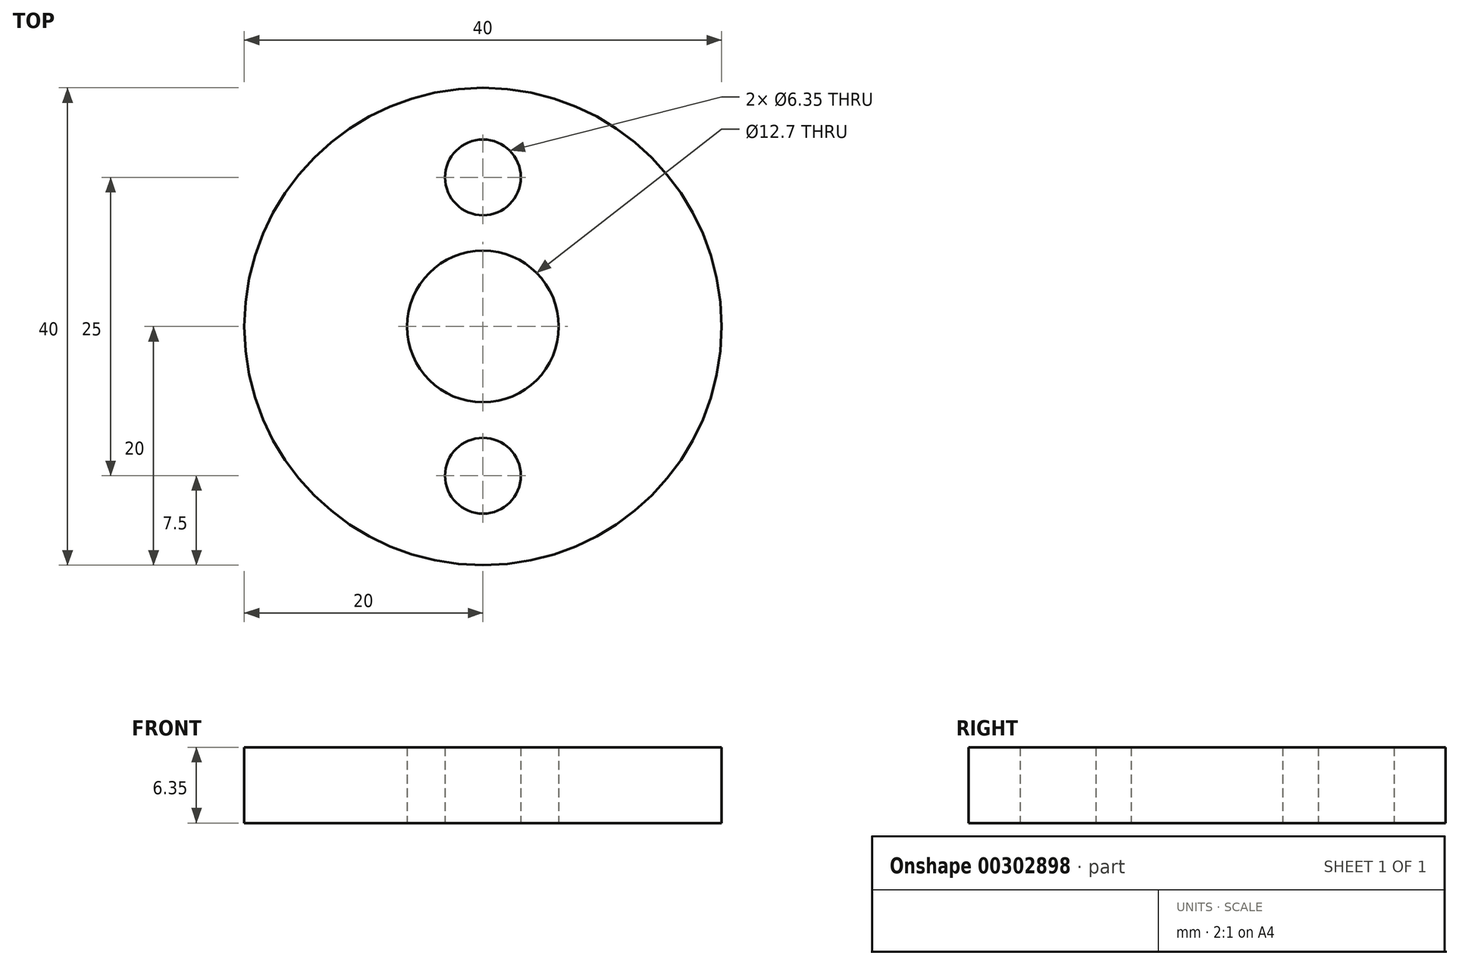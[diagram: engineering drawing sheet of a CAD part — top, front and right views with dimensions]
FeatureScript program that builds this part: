
annotation { "Feature Type Name" : "Feature", "Feature Type Description" : "" }
export const myFeature = defineFeature(function(context is Context, id is Id, definition is map)
    precondition{}
    {
        {
            var Q0;
            Q0=qCreatedBy(makeId("Top.planeOp"),FACE);
            var sketch = newSketch(context, id + "F0", { "sketchPlane" : qUnion([Q0])});
            skCircle(sketch, "E0", {"center": v(0, 0) * mm, "radius": 20 * mm});
            skCircle(sketch, "E1", {"center": v(0, 0) * mm, "radius": 6.35 * mm});
            skSolve(sketch);
        }
        {
            var Q0;
            Q0 = qSketchRegion(id + "F0", true);
            extrude(context, id + "F1", {"entities" : qUnion([Q0]), "depth" : 6.35 * mm});
        }
        {
            var Q0;
            Q0=qCreatedBy(makeId("Top.planeOp"),FACE);
            var sketch = newSketch(context, id + "F2", { "sketchPlane" : qUnion([Q0])});
            skCircle(sketch, "E2", {"center": v(0, 12.5) * mm, "radius": 3.18 * mm});
            skCircle(sketch, "E3", {"center": v(0, -12.5) * mm, "radius": 3.18 * mm});
            skSolve(sketch);
        }
        {
            var Q0;
            Q0 = qSketchRegion(id + "F2", true);
            extrude(context, id + "F3", {"entities" : qUnion([Q0]), "operationType" : NewBodyOperationType.REMOVE, "endBound" : BoundingType.UP_TO_NEXT, "depth" : 25.4 * mm});
        }
    });
